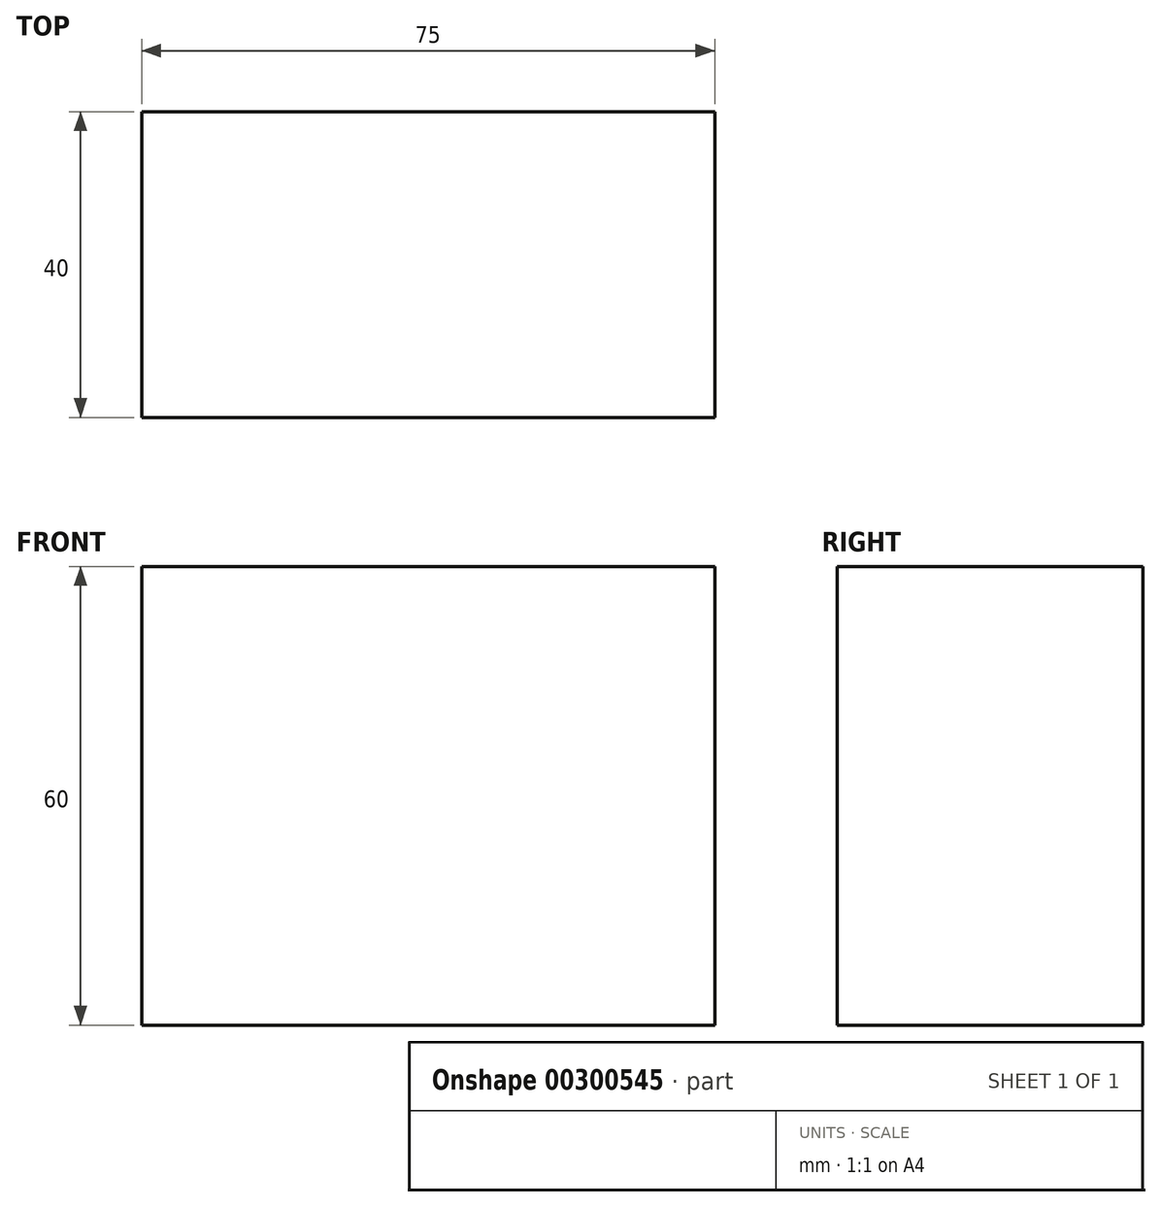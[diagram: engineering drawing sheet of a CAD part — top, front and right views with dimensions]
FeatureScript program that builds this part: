
annotation { "Feature Type Name" : "Feature", "Feature Type Description" : "" }
export const myFeature = defineFeature(function(context is Context, id is Id, definition is map)
    precondition{}
    {
        {
            var Q0;
            Q0=qCreatedBy(makeId("Front.planeOp"),FACE);
            var sketch = newSketch(context, id + "F0", { "sketchPlane" : qUnion([Q0])});
            skLineSegment(sketch, "E0.bottom", {"start": v(38.96, 30) * mm, "end": v(-36.04, 30) * mm});
            skLineSegment(sketch, "E0.top", {"start": v(38.96, -30) * mm, "end": v(-36.04, -30) * mm});
            skLineSegment(sketch, "E0.left", {"start": v(38.96, 30) * mm, "end": v(38.96, -30) * mm});
            skLineSegment(sketch, "E0.right", {"start": v(-36.04, 30) * mm, "end": v(-36.04, -30) * mm});
            skPoint(sketch, "E0.middle", {"position": v(1.46, 0) * mm});
            skSolve(sketch);
        }
        {
            var Q0;
            Q0=makeQuery(id+"F0.imprint","IMPRINT",FACE,{"disambiguationData":[TD([[makeQuery(id+"F0.imprint","IMPRINT",EDGE,{"derivedFrom":sQuery(id+"F0.wireOp",EDGE,"E0.bottom")}),1.0]])]});
            extrude(context, id + "F1", {"entities" : qUnion([Q0]), "depth" : 40 * mm});
        }
    });
